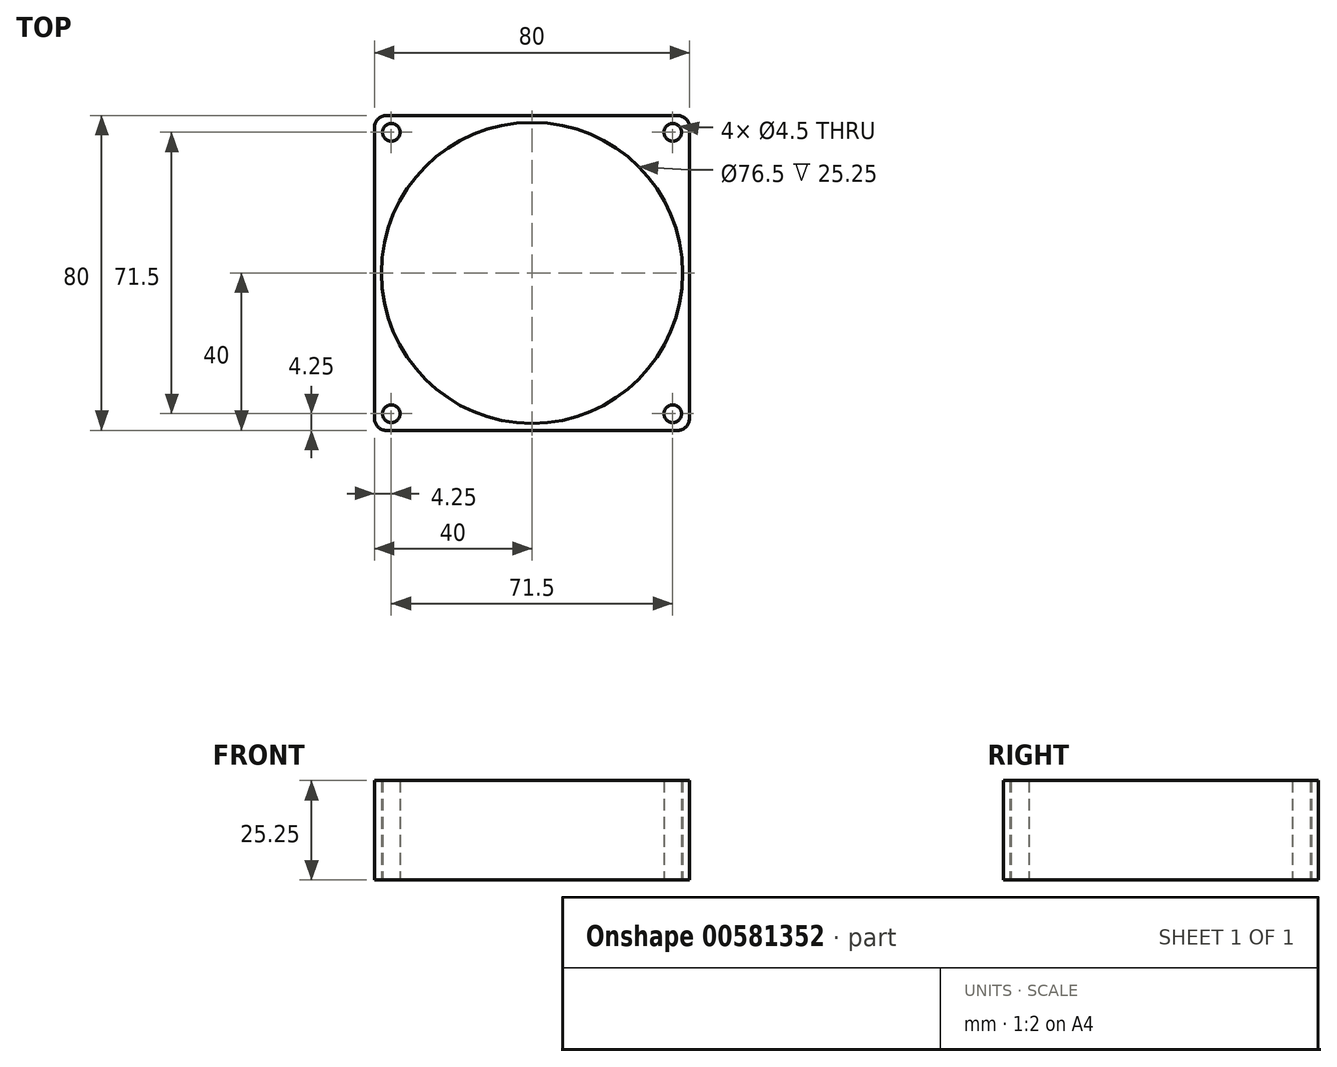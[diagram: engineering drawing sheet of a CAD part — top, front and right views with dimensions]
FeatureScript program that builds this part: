
annotation { "Feature Type Name" : "Feature", "Feature Type Description" : "" }
export const myFeature = defineFeature(function(context is Context, id is Id, definition is map)
    precondition{}
    {
        {
            var Q0;
            Q0=qCreatedBy(makeId("Top.planeOp"),FACE);
            var sketch = newSketch(context, id + "F0", { "sketchPlane" : qUnion([Q0])});
            skLineSegment(sketch, "E0.bottom", {"start": v(37, -40) * mm, "end": v(-37, -40) * mm});
            skLineSegment(sketch, "E0.top", {"start": v(37, 40) * mm, "end": v(-37, 40) * mm});
            skLineSegment(sketch, "E0.left", {"start": v(40, -37) * mm, "end": v(40, 37) * mm});
            skLineSegment(sketch, "E0.right", {"start": v(-40, -37) * mm, "end": v(-40, 37) * mm});
            skPoint(sketch, "E0.middle", {"position": v(0, 0) * mm});
            skPoint(sketch, "E1.visualSharp", {"position": v(-40, 40) * mm});
            skArc(sketch, "E1.filletArc", {"start": v(-37, 40) * mm, "mid": v(-39.12, 39.12) * mm, "end": v(-40, 37) * mm});
            skPoint(sketch, "E2.visualSharp", {"position": v(40, 40) * mm});
            skArc(sketch, "E2.filletArc", {"start": v(40, 37) * mm, "mid": v(39.12, 39.12) * mm, "end": v(37, 40) * mm});
            skPoint(sketch, "E3.visualSharp", {"position": v(40, -40) * mm});
            skArc(sketch, "E3.filletArc", {"start": v(37, -40) * mm, "mid": v(39.12, -39.12) * mm, "end": v(40, -37) * mm});
            skPoint(sketch, "E4.visualSharp", {"position": v(-40, -40) * mm});
            skArc(sketch, "E4.filletArc", {"start": v(-40, -37) * mm, "mid": v(-39.12, -39.12) * mm, "end": v(-37, -40) * mm});
            skCircle(sketch, "E5", {"center": v(-35.75, 35.75) * mm, "radius": 2.25 * mm});
            skCircle(sketch, "E6", {"center": v(35.75, 35.75) * mm, "radius": 2.25 * mm});
            skCircle(sketch, "E7", {"center": v(35.75, -35.75) * mm, "radius": 2.25 * mm});
            skCircle(sketch, "E8", {"center": v(-35.75, -35.75) * mm, "radius": 2.25 * mm});
            skCircle(sketch, "E9", {"center": v(0, 0) * mm, "radius": 38.25 * mm});
            skSolve(sketch);
        }
        {
            var Q0;
            Q0=makeQuery(id+"F0.imprint","IMPRINT",FACE,{"disambiguationData":[TD([[makeQuery(id+"F0.imprint","IMPRINT",EDGE,{"derivedFrom":sQuery(id+"F0.wireOp",EDGE,"E0.bottom")}),-1.0]])]});
            extrude(context, id + "F1", {"entities" : qUnion([Q0]), "depth" : 25.25 * mm, "offsetDistance" : 25 * mm});
        }
        {
            var Q0;
            Q0=qCreatedBy(makeId("Top.planeOp"),FACE);
            var sketch = newSketch(context, id + "F2", { "sketchPlane" : qUnion([Q0])});
            skCircle(sketch, "E10", {"center": v(0, 0) * mm, "radius": 16.5 * mm});
            skSolve(sketch);
        }
        {
            var Q0;
            Q0=makeQuery(id+"F2.imprint","IMPRINT",FACE,{"disambiguationData":[TD([[makeQuery(id+"F2.imprint","IMPRINT",EDGE,{"derivedFrom":sQuery(id+"F2.wireOp",EDGE,"E10")}),1.0]])]});
            var Q1;
            Q1 = qSketchRegion(id + "F2", true);
            extrude(context, id + "F3", {"entities" : qUnion([Q0, Q1]), "depth" : 25.25 * mm, "offsetDistance" : 25 * mm});
        }
        {
            var Q0;
            Q0=makeQuery(id+"F3.opExtrude","SWEPT_BODY",BODY,{"disambiguationData":[OSD([sQuery(id+"F2.wireOp",EDGE,"E10")])]});
            deleteBodies(context, id + "F4", {"entities" : qUnion([Q0])});
        }
    });
